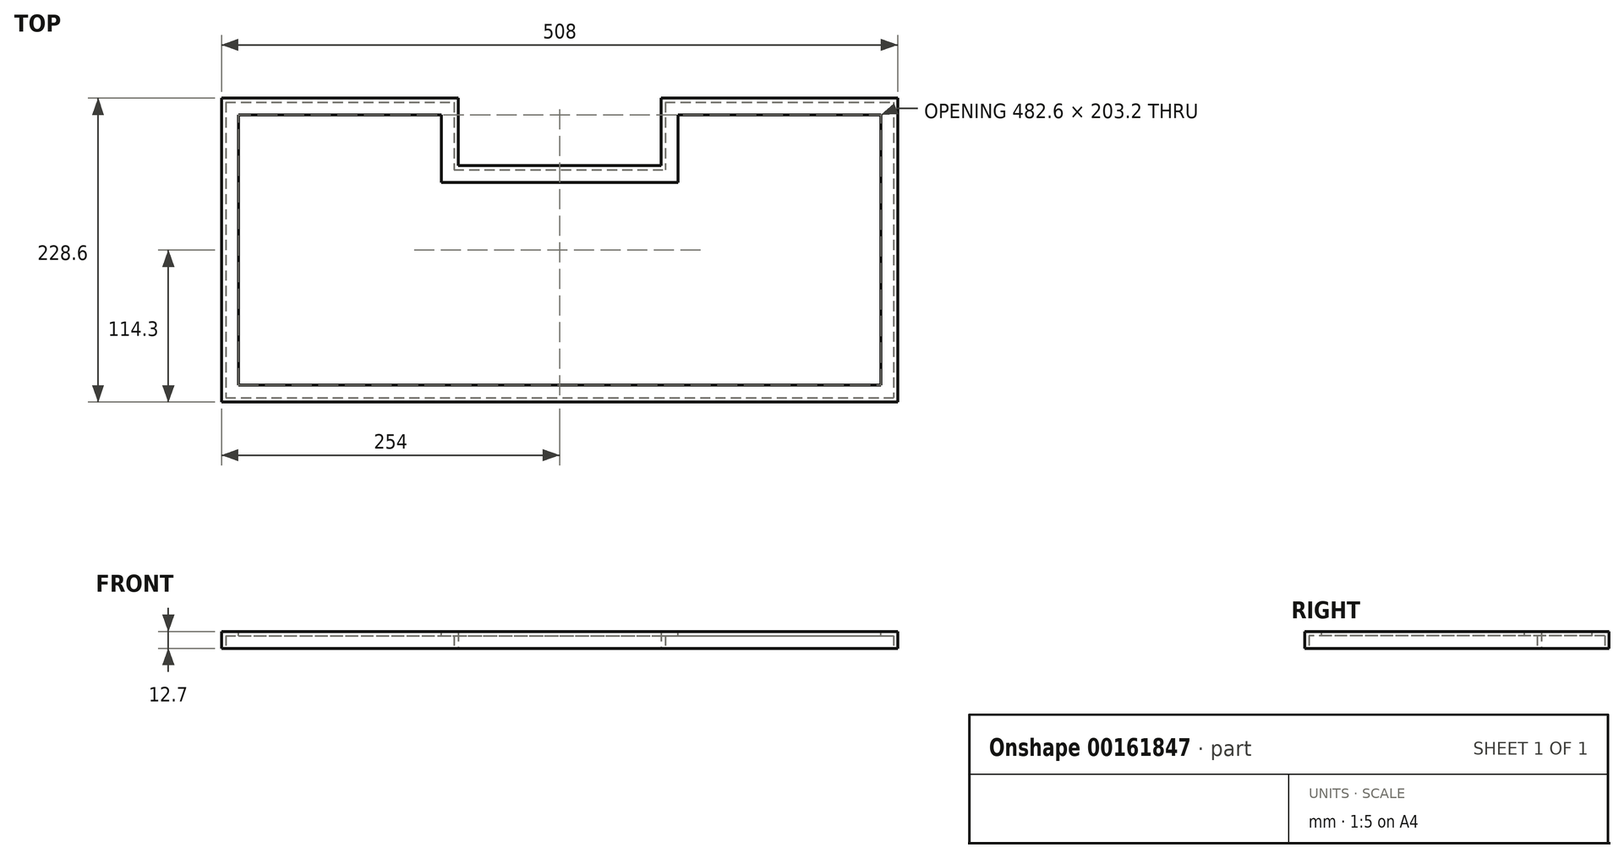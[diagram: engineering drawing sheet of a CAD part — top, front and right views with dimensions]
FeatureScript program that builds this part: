
annotation { "Feature Type Name" : "Feature", "Feature Type Description" : "" }
export const myFeature = defineFeature(function(context is Context, id is Id, definition is map)
    precondition{}
    {
        {
            var Q0;
            Q0=qCreatedBy(makeId("Top.planeOp"),FACE);
            var sketch = newSketch(context, id + "F0", { "sketchPlane" : qUnion([Q0])});
            skLineSegment(sketch, "E0.bottom", {"start": v(0, 0) * mm, "end": v(152.4, 0) * mm});
            skLineSegment(sketch, "E0.top", {"start": v(0, -101.6) * mm, "end": v(152.4, -101.6) * mm});
            skLineSegment(sketch, "E0.left", {"start": v(0, 0) * mm, "end": v(0, -101.6) * mm});
            skLineSegment(sketch, "E0.right", {"start": v(152.4, 0) * mm, "end": v(152.4, -101.6) * mm});
            skLineSegment(sketch, "E1.0", {"start": v(-177.8, 177.8) * mm, "end": v(330.2, 177.8) * mm});
            skLineSegment(sketch, "E1.1", {"start": v(-177.8, 177.8) * mm, "end": v(-177.8, -279.4) * mm});
            skLineSegment(sketch, "E1.2", {"start": v(-177.8, -279.4) * mm, "end": v(330.2, -279.4) * mm});
            skLineSegment(sketch, "E1.3", {"start": v(330.2, 177.8) * mm, "end": v(330.2, -279.4) * mm});
            skSolve(sketch);
        }
        {
            var Q0;
            Q0 = qSketchRegion(id + "F0", true);
            extrude(context, id + "F1", {"entities" : qUnion([Q0]), "depth" : 12.7 * mm});
        }
        {
            var Q0;
            Q0=makeQuery(id+"F1.opExtrude","CAP_FACE",FACE,{"disambiguationData":[OSD([sQuery(id+"F0.wireOp",EDGE,"E0.bottom"),sQuery(id+"F0.wireOp",EDGE,"E0.top"),sQuery(id+"F0.wireOp",EDGE,"E0.left"),sQuery(id+"F0.wireOp",EDGE,"E0.right"),sQuery(id+"F0.wireOp",EDGE,"E1.0"),sQuery(id+"F0.wireOp",EDGE,"E1.1"),sQuery(id+"F0.wireOp",EDGE,"E1.2"),sQuery(id+"F0.wireOp",EDGE,"E1.3")])],"isStart":false});
            var sketch = newSketch(context, id + "F2", { "sketchPlane" : qUnion([Q0])});
            skLineSegment(sketch, "E2.bottom", {"start": v(-177.8, -50.8) * mm, "end": v(330.2, -50.8) * mm});
            skLineSegment(sketch, "E2.top", {"start": v(-177.8, 177.8) * mm, "end": v(330.2, 177.8) * mm});
            skLineSegment(sketch, "E2.left", {"start": v(-177.8, -50.8) * mm, "end": v(-177.8, 177.8) * mm});
            skLineSegment(sketch, "E2.right", {"start": v(330.2, -50.8) * mm, "end": v(330.2, 177.8) * mm});
            skSolve(sketch);
        }
        {
            var Q0;
            Q0 = qSketchRegion(id + "F2", true);
            extrude(context, id + "F3", {"entities" : qUnion([Q0]), "operationType" : NewBodyOperationType.REMOVE, "endBound" : BoundingType.THROUGH_ALL, "oppositeDirection" : true, "depth" : 25.4 * mm});
        }
        {
            var Q0;
            Q0=makeQuery(id+"F1.opExtrude","CAP_FACE",FACE,{"disambiguationData":[OSD([sQuery(id+"F0.wireOp",EDGE,"E0.bottom"),sQuery(id+"F0.wireOp",EDGE,"E0.top"),sQuery(id+"F0.wireOp",EDGE,"E0.left"),sQuery(id+"F0.wireOp",EDGE,"E0.right"),sQuery(id+"F0.wireOp",EDGE,"E1.0"),sQuery(id+"F0.wireOp",EDGE,"E1.1"),sQuery(id+"F0.wireOp",EDGE,"E1.2"),sQuery(id+"F0.wireOp",EDGE,"E1.3")])],"isStart":false});
            var sketch = newSketch(context, id + "F4", { "sketchPlane" : qUnion([Q0])});
            skLineSegment(sketch, "E3.0", {"start": v(-165.1, -63.5) * mm, "end": v(-165.1, -266.7) * mm});
            skLineSegment(sketch, "E3.1", {"start": v(-165.1, -266.7) * mm, "end": v(317.5, -266.7) * mm});
            skLineSegment(sketch, "E3.2", {"start": v(-165.1, -63.5) * mm, "end": v(-12.7, -63.5) * mm});
            skLineSegment(sketch, "E3.3", {"start": v(317.5, -63.5) * mm, "end": v(317.5, -266.7) * mm});
            skLineSegment(sketch, "E3.4", {"start": v(-12.7, -63.5) * mm, "end": v(-12.7, -114.3) * mm});
            skLineSegment(sketch, "E3.5", {"start": v(-12.7, -114.3) * mm, "end": v(165.1, -114.3) * mm});
            skLineSegment(sketch, "E3.6", {"start": v(165.1, -63.5) * mm, "end": v(165.1, -114.3) * mm});
            skLineSegment(sketch, "E3.7", {"start": v(165.1, -63.5) * mm, "end": v(317.5, -63.5) * mm});
            skSolve(sketch);
        }
        {
            var Q0;
            Q0 = qSketchRegion(id + "F4", true);
            extrude(context, id + "F5", {"entities" : qUnion([Q0]), "operationType" : NewBodyOperationType.REMOVE, "endBound" : BoundingType.THROUGH_ALL, "oppositeDirection" : true, "depth" : 25.4 * mm});
        }
        {
            var Q0;
            Q0=makeQuery(id+"F1.opExtrude","CAP_FACE",FACE,{"disambiguationData":[OSD([sQuery(id+"F0.wireOp",EDGE,"E0.bottom"),sQuery(id+"F0.wireOp",EDGE,"E0.top"),sQuery(id+"F0.wireOp",EDGE,"E0.left"),sQuery(id+"F0.wireOp",EDGE,"E0.right"),sQuery(id+"F0.wireOp",EDGE,"E1.0"),sQuery(id+"F0.wireOp",EDGE,"E1.1"),sQuery(id+"F0.wireOp",EDGE,"E1.2"),sQuery(id+"F0.wireOp",EDGE,"E1.3")])],"isStart":true});
            var sketch = newSketch(context, id + "F6", { "sketchPlane" : qUnion([Q0])});
            skLineSegment(sketch, "E4.0", {"start": v(-174.63, 53.97) * mm, "end": v(-174.63, 276.23) * mm});
            skLineSegment(sketch, "E4.1", {"start": v(-174.63, 53.97) * mm, "end": v(-3.17, 53.97) * mm});
            skLineSegment(sketch, "E4.2", {"start": v(-174.63, 276.23) * mm, "end": v(327.03, 276.23) * mm});
            skLineSegment(sketch, "E4.3", {"start": v(-3.17, 53.97) * mm, "end": v(-3.17, 104.77) * mm});
            skLineSegment(sketch, "E4.4", {"start": v(327.03, 53.97) * mm, "end": v(327.03, 276.23) * mm});
            skLineSegment(sketch, "E4.5", {"start": v(155.57, 53.97) * mm, "end": v(327.03, 53.97) * mm});
            skLineSegment(sketch, "E4.6", {"start": v(155.57, 53.97) * mm, "end": v(155.57, 104.77) * mm});
            skLineSegment(sketch, "E4.7", {"start": v(-3.17, 104.77) * mm, "end": v(155.57, 104.77) * mm});
            skSolve(sketch);
        }
        {
            var Q0;
            Q0 = qSketchRegion(id + "F6", true);
            extrude(context, id + "F7", {"entities" : qUnion([Q0]), "operationType" : NewBodyOperationType.REMOVE, "oppositeDirection" : true, "depth" : 9.52 * mm});
        }
    });
